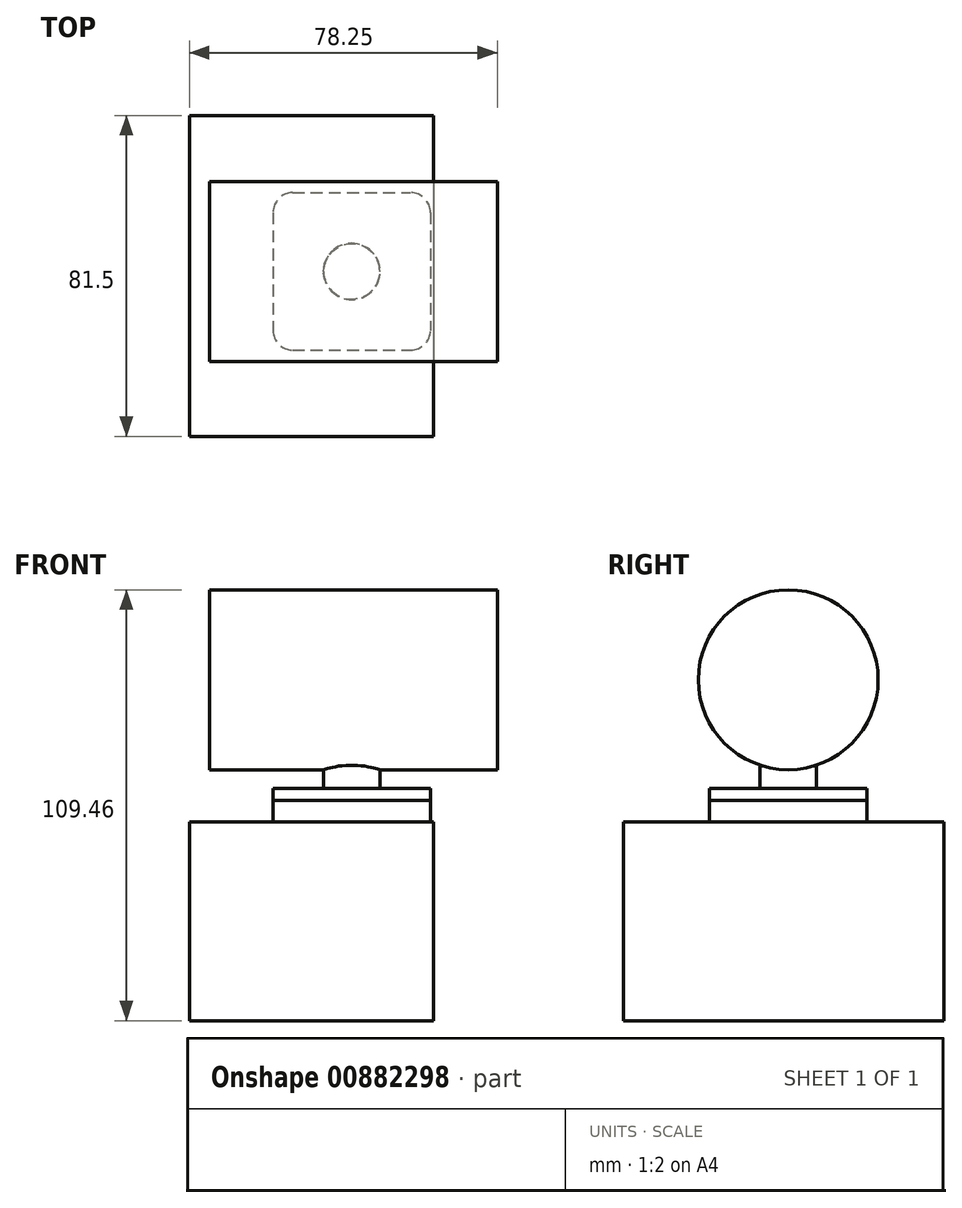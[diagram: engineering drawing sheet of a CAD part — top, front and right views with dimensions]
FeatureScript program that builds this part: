
annotation { "Feature Type Name" : "Feature", "Feature Type Description" : "" }
export const myFeature = defineFeature(function(context is Context, id is Id, definition is map)
    precondition{}
    {
        {
            var Q0;
            Q0=qCreatedBy(makeId("Top.planeOp"),FACE);
            var sketch = newSketch(context, id + "F0", { "sketchPlane" : qUnion([Q0])});
            skLineSegment(sketch, "E0.bottom", {"start": v(-31, 40.75) * mm, "end": v(31, 40.75) * mm});
            skLineSegment(sketch, "E0.top", {"start": v(-31, -40.75) * mm, "end": v(31, -40.75) * mm});
            skLineSegment(sketch, "E0.left", {"start": v(-31, 40.75) * mm, "end": v(-31, -40.75) * mm});
            skLineSegment(sketch, "E0.right", {"start": v(31, 40.75) * mm, "end": v(31, -40.75) * mm});
            skPoint(sketch, "E1", {"position": v(0, 40.75) * mm});
            skPoint(sketch, "E2", {"position": v(31, 0) * mm});
            skSolve(sketch);
        }
        {
            var Q0;
            Q0=makeQuery(id+"F0.imprint","IMPRINT",FACE,{"disambiguationData":[TD([[makeQuery(id+"F0.imprint","IMPRINT",EDGE,{"derivedFrom":sQuery(id+"F0.wireOp",EDGE,"E0.bottom")}),-1.0]])]});
            extrude(context, id + "F1", {"entities" : qUnion([Q0]), "depth" : 50.5 * mm, "offsetDistance" : 25.4 * mm});
        }
        {
            var Q0;
            Q0=makeQuery(id+"F1.opExtrude","CAP_FACE",FACE,{"disambiguationData":[OSD([sQuery(id+"F0.wireOp",EDGE,"E0.bottom"),sQuery(id+"F0.wireOp",EDGE,"E0.top"),sQuery(id+"F0.wireOp",EDGE,"E0.left"),sQuery(id+"F0.wireOp",EDGE,"E0.right")])],"isStart":false});
            var sketch = newSketch(context, id + "F2", { "sketchPlane" : qUnion([Q0])});
            skLineSegment(sketch, "E3.bottom", {"start": v(-9.75, 21.15) * mm, "end": v(30.25, 21.15) * mm});
            skLineSegment(sketch, "E3.top", {"start": v(-9.75, -18.85) * mm, "end": v(30.25, -18.85) * mm});
            skLineSegment(sketch, "E3.left", {"start": v(-9.75, 21.15) * mm, "end": v(-9.75, -18.85) * mm});
            skLineSegment(sketch, "E3.right", {"start": v(30.25, 21.15) * mm, "end": v(30.25, -18.85) * mm});
            skSolve(sketch);
        }
        {
            var Q0;
            Q0=makeQuery(id+"F2.imprint","IMPRINT",FACE,{"disambiguationData":[TD([[makeQuery(id+"F2.imprint","IMPRINT",EDGE,{"derivedFrom":sQuery(id+"F2.wireOp",EDGE,"E3.bottom")}),-1.0]])]});
            extrude(context, id + "F3", {"entities" : qUnion([Q0]), "operationType" : NewBodyOperationType.ADD, "depth" : 5.45 * mm, "offsetDistance" : 25.4 * mm});
        }
        {
            var Q0;
            Q0=makeQuery(id+"F3.opExtrude","SWEPT_EDGE",EDGE,{"disambiguationData":[OSD([sQuery(id+"F2.wireOp",EDGE,"E3.bottom"),sQuery(id+"F2.wireOp",EDGE,"E3.left")])]});
            var Q1;
            Q1=makeQuery(id+"F3.opExtrude","SWEPT_EDGE",EDGE,{"disambiguationData":[OSD([sQuery(id+"F2.wireOp",EDGE,"E3.top"),sQuery(id+"F2.wireOp",EDGE,"E3.left")])]});
            var Q2;
            Q2=makeQuery(id+"F3.opExtrude","SWEPT_EDGE",EDGE,{"disambiguationData":[OSD([sQuery(id+"F2.wireOp",EDGE,"E3.top"),sQuery(id+"F2.wireOp",EDGE,"E3.right")])]});
            var Q3;
            Q3=makeQuery(id+"F3.opExtrude","SWEPT_EDGE",EDGE,{"disambiguationData":[OSD([sQuery(id+"F2.wireOp",EDGE,"E3.bottom"),sQuery(id+"F2.wireOp",EDGE,"E3.right")])]});
            fillet(context, id + "F4", {"entities" : qUnion([Q0, Q1, Q2, Q3]), "radius" : 5 * mm, "tangentPropagation" : true, "allowEdgeOverflow" : false});
        }
        {
            var Q0;
            Q0=makeQuery(id+"F3.opExtrude","CAP_FACE",FACE,{"disambiguationData":[OSD([sQuery(id+"F2.wireOp",EDGE,"E3.bottom"),sQuery(id+"F2.wireOp",EDGE,"E3.top"),sQuery(id+"F2.wireOp",EDGE,"E3.left"),sQuery(id+"F2.wireOp",EDGE,"E3.right")])],"isStart":false});
            extrude(context, id + "F5", {"entities" : qUnion([Q0]), "depth" : 3 * mm, "offsetDistance" : 25 * mm});
        }
        {
            var Q0;
            Q0=makeQuery(id+"F5.opExtrude","CAP_FACE",FACE,{"disambiguationData":[OSD([sQuery(id+"F2.wireOp",EDGE,"E3.bottom"),sQuery(id+"F2.wireOp",EDGE,"E3.top"),sQuery(id+"F2.wireOp",EDGE,"E3.left"),sQuery(id+"F2.wireOp",EDGE,"E3.right")])],"isStart":false});
            var sketch = newSketch(context, id + "F6", { "sketchPlane" : qUnion([Q0])});
            skLineSegment(sketch, "E4", {"start": v(-9.75, 1.15) * mm, "end": v(30.25, 1.15) * mm, "construction": true});
            skLineSegment(sketch, "E5", {"start": v(10.25, 21.15) * mm, "end": v(10.25, -18.85) * mm});
            skCircle(sketch, "E6", {"center": v(10.25, 1.15) * mm, "radius": 7.15 * mm});
            skSolve(sketch);
        }
        {
            var Q0;
            {var subQ0=sQuery(id+"F6.wireOp",EDGE,"E6");var subQ1=sQuery(id+"F6.wireOp",EDGE,"E5");var subQ2=makeQuery(id+"F6.imprint","INTERSECT",VERTEX,{"disambiguationData":[OD(0.0)],"derivedFrom":[subQ1,subQ0]});Q0=makeQuery(id+"F6.imprint","IMPRINT",FACE,{"disambiguationData":[TD([[makeQuery(id+"F6.imprint","IMPRINT",EDGE,{"disambiguationData":[TD([[subQ2,-1.0]])],"derivedFrom":subQ1}),1.0]])]});}
            var Q1;
            {var subQ0=sQuery(id+"F6.wireOp",EDGE,"E6");var subQ1=sQuery(id+"F6.wireOp",EDGE,"E5");var subQ2=makeQuery(id+"F6.imprint","INTERSECT",VERTEX,{"disambiguationData":[OD(0.0)],"derivedFrom":[subQ1,subQ0]});Q1=makeQuery(id+"F6.imprint","IMPRINT",FACE,{"disambiguationData":[TD([[makeQuery(id+"F6.imprint","IMPRINT",EDGE,{"disambiguationData":[TD([[subQ2,-1.0]])],"derivedFrom":subQ1}),-1.0]])]});}
            extrude(context, id + "F7", {"entities" : qUnion([Q0, Q1]), "operationType" : NewBodyOperationType.ADD, "depth" : 10 * mm, "offsetDistance" : 25 * mm});
        }
        {
            var Q0;
            Q0=makeQuery(id+"F7.opExtrude","CAP_FACE",FACE,{"disambiguationData":[OSD([sQuery(id+"F6.wireOp",EDGE,"E6")])],"isStart":false});
            var sketch = newSketch(context, id + "F8", { "sketchPlane" : qUnion([Q0])});
            skLineSegment(sketch, "E7", {"start": v(10.25, 1.15) * mm, "end": v(3.1, 1.15) * mm});
            skLineSegment(sketch, "E8", {"start": v(10.25, 1.15) * mm, "end": v(17.4, 1.15) * mm});
            skSolve(sketch);
        }
        {
            var Q0;
            Q0=makeQuery(id+"F5.opExtrude","CAP_FACE",FACE,{"disambiguationData":[OSD([sQuery(id+"F2.wireOp",EDGE,"E3.bottom"),sQuery(id+"F2.wireOp",EDGE,"E3.top"),sQuery(id+"F2.wireOp",EDGE,"E3.left"),sQuery(id+"F2.wireOp",EDGE,"E3.right")])],"isStart":false});
            var sketch = newSketch(context, id + "F9", { "sketchPlane" : qUnion([Q0])});
            skPoint(sketch, "E9.0", {"position": v(10.25, 1.15) * mm});
            skPoint(sketch, "E10.0", {"position": v(17.4, 1.15) * mm});
            skPoint(sketch, "E11.0", {"position": v(3.1, 1.15) * mm});
            skLineSegment(sketch, "E12", {"start": v(3.1, 1.15) * mm, "end": v(17.4, 1.15) * mm, "construction": true});
            skSolve(sketch);
        }
        {
            var Q0;
            Q0=sQuery(id+"F8.wireOp",VERTEX,"E7.start");
            var Q1;
            Q1=sQuery(id+"F9.wireOp",VERTEX,"E9.0");
            var Q2;
            Q2=sQuery(id+"F9.wireOp",VERTEX,"E10.0");
            cPlane(context, id + "F10", {"entities" : qUnion([Q0, Q1, Q2]), "cplaneType" : CPlaneType.THREE_POINT, "offset" : 25 * mm, "width" : 150 * mm, "height" : 150 * mm});
        }
        {
            var Q0;
            Q0=qCreatedBy(id+"F10.planeOp",FACE);
            var sketch = newSketch(context, id + "F11", { "sketchPlane" : qUnion([Q0])});
            skLineSegment(sketch, "E13", {"start": v(25.85, 86.6) * mm, "end": v(-47.25, 86.6) * mm, "construction": true});
            skLineSegment(sketch, "E14", {"start": v(25.85, 63.76) * mm, "end": v(25.85, 109.46) * mm});
            skPoint(sketch, "E15", {"position": v(25.85, 86.6) * mm});
            skLineSegment(sketch, "E16", {"start": v(25.85, 109.46) * mm, "end": v(-47.25, 109.46) * mm});
            skLineSegment(sketch, "E17", {"start": v(-47.25, 86.6) * mm, "end": v(-47.25, 109.46) * mm});
            skLineSegment(sketch, "E18", {"start": v(25.85, 86.6) * mm, "end": v(-47.25, 86.6) * mm});
            skPoint(sketch, "E19", {"position": v(11.85, 86.61) * mm});
            skPoint(sketch, "E20", {"position": v(8.55, 86.61) * mm});
            skPoint(sketch, "E21", {"position": v(-4.14, 86.61) * mm});
            skPoint(sketch, "E22", {"position": v(-24.14, 86.61) * mm});
            skSolve(sketch);
        }
        {
            var Q0;
            {var subQ0=sQuery(id+"F11.wireOp",EDGE,"E16");Q0=makeQuery(id+"F11.imprint","IMPRINT",FACE,{"disambiguationData":[TD([[makeQuery(id+"F11.imprint","IMPRINT",EDGE,{"derivedFrom":subQ0}),1.0]])]});}
            var Q1;
            Q1=sQuery(id+"F11.wireOp",EDGE,"E18");
            revolve(context, id + "F12", {"operationType" : NewBodyOperationType.ADD, "surfaceOperationType" : NewSurfaceOperationType.NEW, "entities" : qUnion([Q0]), "axis" : qUnion([Q1]), "revolveType" : RevolveType.FULL});
        }
    });
